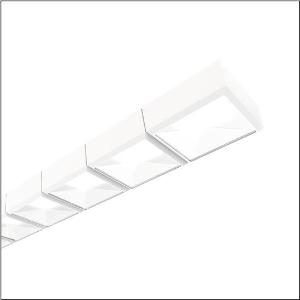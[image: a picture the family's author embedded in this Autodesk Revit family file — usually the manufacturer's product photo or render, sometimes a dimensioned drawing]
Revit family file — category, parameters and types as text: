
# Revit family: scriptus_r__11_5mz323d04wa_1206
name_source: partatom
category: Lighting Fixtures
units: mm (PartAtom-declared; Revit-internal decimal feet)

## family parameters
Cut with Voids When Loaded = No
Host = Face
Light Source = No
Part Type = Normal
Room Calculation Point = No
Round Connector Dimension = Use Diameter
Shared = No

## types (1)
- Scriptus® 11 (1 x LED 4000K / CRI = 80 (unbekannt), 4840 lm / 7230 lm, 4000K)
    Apparent Load = 91 VA
    CIE Flux Codes = - - - 0 100 / 82 95 99 100 100
    Color Rendering = 80
    Color Temperature = 4000K
    Default Elevation = 1800 mm
    Description = Scriptus® 11, office luminaire, primary optical cover: lenses, CAT 2 (L<= 3000cd/m²), light emission: direct/indirect distribution, primary light characteristic: symmetric, installation type: suspended mounting, LED, rated luminous flux: 12.070lm, luminous efficacy: 133lm/W, light colour: 840, colour temperature: 4000K, control gear: ECG DALI, with terminal, 5-pole, mains connection: 230V, AC, 50Hz, rated input power: 91W, LED, control gear: ECG DALI, housing, luminaire housing, of aluminium, traffic white (RAL 9016), length: 2.426mm, width: 114mm, height: 57mm, protection rating (complete): IP20, insulation class (complete): insulation class I (protective earthing), certification: CE, ENEC, VDE, protection symbol: F, permissible operating ambient temperature: 0..+35°C, standard: EN 50419, packaging unit: 1 piece
    Height = 57 mm
    Lamp = 1 x LED 4000K / CRI >= 80 (unbekannt)
    Lamp Light Flux = 4840 lm / 7230 lm
    Lamp count = 1
    Length = 2426 mm
    Luminous efficacy = 133 lm/W
    Manufacturer = Siteco
    ModVariant = No
    Model = 5MZ323D04WA
    Mounting Place = Ceiling
    Mounting Type = Pendant
    Number of Poles = 1
    OnlyDefault = Yes
    Power Factor = 1
    Product Name = Scriptus® 11
    Product group = office luminaire | ceiling pendant
    ProductGroupID = 902
    Protection Class = Protection class I
    Protection Degree = IP 20
    RLX_Detail_Level = 1
    RLX_Emergency_Light_Flux = 0 lm
    RLX_Emergency_Type = 0
    RLX_Emergency_Type_DB = No
    RlxData = <blob elided: 30117 chars, md5=c28847d7>
    Socket = socket
    Standby Power = 0 W
    System Light Flux = 12070 lm
    System Power = 91 W
    Type Comments = Product without accessories
    Type Image = l_1004839.jpg
    URL = http://relux.com
    VarID = ---
    Voltage = 0 V
    Weight = 0.00 kg
    Width = 114 mm

## geometry (parser evidence)
native form markers: Blend x4, Sweep x12
no freeform markers — native parametric forms only
